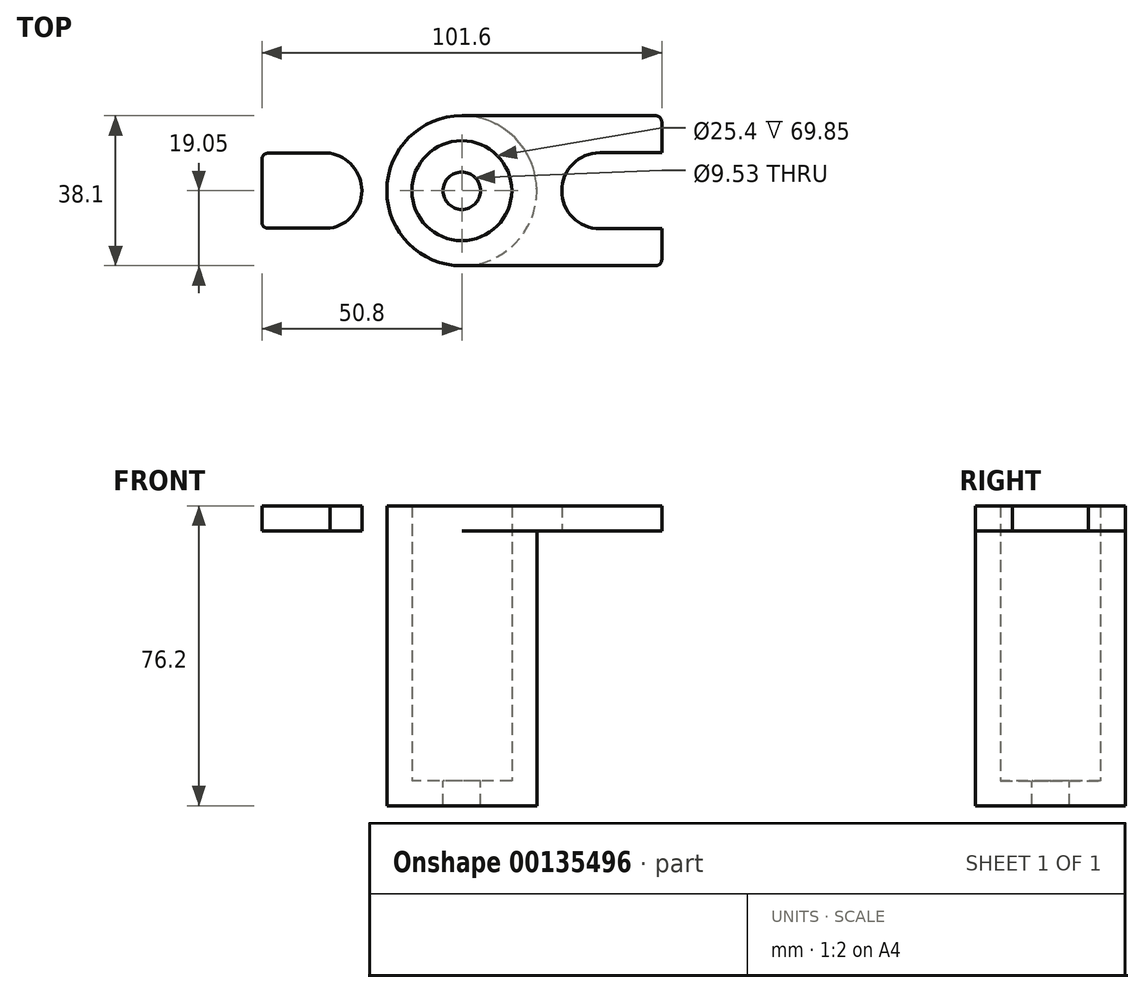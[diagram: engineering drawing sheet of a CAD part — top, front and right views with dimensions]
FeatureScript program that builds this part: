
annotation { "Feature Type Name" : "Feature", "Feature Type Description" : "" }
export const myFeature = defineFeature(function(context is Context, id is Id, definition is map)
    precondition{}
    {
        {
            var Q0;
            Q0=qCreatedBy(makeId("Top.planeOp"),FACE);
            var sketch = newSketch(context, id + "F0", { "sketchPlane" : qUnion([Q0])});
            skLineSegment(sketch, "E0.bottom", {"start": v(0, 0) * mm, "end": v(101.6, 0) * mm});
            skLineSegment(sketch, "E0.top", {"start": v(0, 38.1) * mm, "end": v(101.6, 38.1) * mm});
            skLineSegment(sketch, "E0.left", {"start": v(0, 0) * mm, "end": v(0, 38.1) * mm});
            skLineSegment(sketch, "E0.right", {"start": v(101.6, 0) * mm, "end": v(101.6, 38.1) * mm});
            skLineSegment(sketch, "E1", {"start": v(0, 19.05) * mm, "end": v(101.6, 19.05) * mm, "construction": true});
            skLineSegment(sketch, "E2", {"start": v(50.8, 38.1) * mm, "end": v(50.8, 0) * mm, "construction": true});
            skCircle(sketch, "E3", {"center": v(50.8, 19.05) * mm, "radius": 4.76 * mm});
            skCircle(sketch, "E4", {"center": v(50.8, 19.05) * mm, "radius": 12.7 * mm});
            skCircle(sketch, "E5", {"center": v(50.8, 19.05) * mm, "radius": 19.05 * mm});
            skArc(sketch, "E6", {"start": v(17.3, 28.58) * mm, "mid": v(25.4, 19.05) * mm, "end": v(17.3, 9.52) * mm});
            skLineSegment(sketch, "E7", {"start": v(0, 28.58) * mm, "end": v(17.3, 28.58) * mm});
            skLineSegment(sketch, "E8", {"start": v(0, 9.52) * mm, "end": v(17.3, 9.52) * mm});
            skArc(sketch, "E9", {"start": v(85.85, 28.7) * mm, "mid": v(76.2, 19.05) * mm, "end": v(85.85, 9.4) * mm});
            skLineSegment(sketch, "E10", {"start": v(85.85, 28.7) * mm, "end": v(101.6, 28.7) * mm});
            skLineSegment(sketch, "E11", {"start": v(85.85, 9.4) * mm, "end": v(101.6, 9.4) * mm});
            skSolve(sketch);
        }
        {
            var Q0;
            Q0=makeQuery(id+"F0.imprint","IMPRINT",FACE,{"disambiguationData":[TD([[makeQuery(id+"F0.imprint","IMPRINT",EDGE,{"derivedFrom":sQuery(id+"F0.wireOp",EDGE,"E6")}),1.0]])]});
            extrude(context, id + "F1", {"entities" : qUnion([Q0]), "depth" : 6.35 * mm});
        }
        {
            var Q0;
            Q0=makeQuery(id+"F0.imprint","IMPRINT",FACE,{"disambiguationData":[TD([[makeQuery(id+"F0.imprint","IMPRINT",EDGE,{"derivedFrom":sQuery(id+"F0.wireOp",EDGE,"E9")}),-1.0]])]});
            extrude(context, id + "F2", {"entities" : qUnion([Q0]), "operationType" : NewBodyOperationType.ADD, "depth" : 6.35 * mm});
        }
        {
            var Q0;
            Q0=makeQuery(id+"F0.imprint","IMPRINT",FACE,{"disambiguationData":[TD([[makeQuery(id+"F0.imprint","IMPRINT",EDGE,{"derivedFrom":sQuery(id+"F0.wireOp",EDGE,"E4")}),-1.0]])]});
            extrude(context, id + "F3", {"entities" : qUnion([Q0]), "operationType" : NewBodyOperationType.ADD, "depth" : 6.35 * mm, "hasSecondDirection" : true, "secondDirectionOppositeDirection" : true, "secondDirectionDepth" : 69.85 * mm});
        }
        {
            var Q0;
            Q0=makeQuery(id+"F0.imprint","IMPRINT",FACE,{"disambiguationData":[TD([[makeQuery(id+"F0.imprint","IMPRINT",EDGE,{"derivedFrom":sQuery(id+"F0.wireOp",EDGE,"E3")}),-1.0]])]});
            extrude(context, id + "F4", {"entities" : qUnion([Q0]), "operationType" : NewBodyOperationType.REMOVE, "depth" : 6.35 * mm, "hasSecondDirection" : true, "secondDirectionOppositeDirection" : true, "secondDirectionDepth" : 57.15 * mm});
        }
        {
            var Q0;
            Q0=makeQuery(id+"F0.imprint","IMPRINT",FACE,{"disambiguationData":[TD([[makeQuery(id+"F0.imprint","IMPRINT",EDGE,{"derivedFrom":sQuery(id+"F0.wireOp",EDGE,"E3")}),-1.0]])]});
            extrude(context, id + "F5", {"entities" : qUnion([Q0]), "operationType" : NewBodyOperationType.ADD, "oppositeDirection" : true, "depth" : 69.85 * mm, "hasSecondDirection" : true, "secondDirectionOppositeDirection" : true, "secondDirectionDepth" : 63.5 * mm});
        }
        {
            var Q0;
            Q0=makeQuery(id+"F2.opExtrude","SWEPT_EDGE",EDGE,{"disambiguationData":[OSD([sQuery(id+"F0.wireOp",EDGE,"E0.bottom"),sQuery(id+"F0.wireOp",EDGE,"E0.right")])]});
            var Q1;
            Q1=makeQuery(id+"F1.opExtrude","SWEPT_EDGE",EDGE,{"disambiguationData":[OSD([sQuery(id+"F0.wireOp",EDGE,"E0.bottom"),sQuery(id+"F0.wireOp",EDGE,"E0.left")])]});
            var Q2;
            Q2=makeQuery(id+"F2.opExtrude","SWEPT_EDGE",EDGE,{"disambiguationData":[OSD([sQuery(id+"F0.wireOp",EDGE,"E0.top"),sQuery(id+"F0.wireOp",EDGE,"E0.right")])]});
            var Q3;
            Q3=makeQuery(id+"F1.opExtrude","SWEPT_EDGE",EDGE,{"disambiguationData":[OSD([sQuery(id+"F0.wireOp",EDGE,"E0.top"),sQuery(id+"F0.wireOp",EDGE,"E0.left")])]});
            fillet(context, id + "F6", {"entities" : qUnion([Q0, Q1, Q2, Q3]), "radius" : 1.52 * mm, "tangentPropagation" : true, "allowEdgeOverflow" : false});
        }
    });
